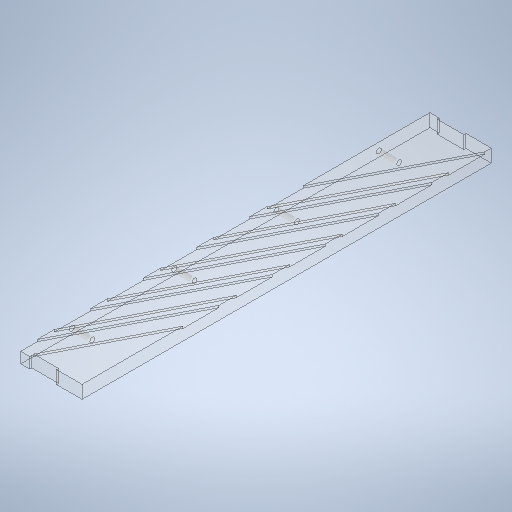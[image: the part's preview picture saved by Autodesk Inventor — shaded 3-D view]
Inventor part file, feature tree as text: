
AUTODESK INVENTOR PART (.ipt)
format: ipt  version: 2025 (Build 290162000, 162)  size: 355,840 bytes
history: native  units: in
note: dims shown in document units (in); Inventor stores cm internally (conversion verified against a paired STEP export)
features: sketch x6, extrude x4, hole x1
ambient origin geometry x8: Origin, YZ Plane, XZ Plane, XY Plane, X Axis, Y Axis, Z Axis, Center Point
bodies: Body1 (feature_tree)
feature tree (11):
  extrude  "Extrusion2"  Depth=7.874in
  extrude  "Extrusion4"  Depth=0.25in
  extrude  "Extrusion6"  Depth=0.0394in TaperAngle=0.0deg
  extrude  "Extrusion7"  Depth=0.3937in
  hole  "Hole1"  [1 undecoded]
  sketch  "Sketch3"  dims[d9=0.25in d10=0.0in d23=0.1855in]
  sketch  "Sketch5"  dims[d25=0.315in d33=0.0394in d34=0.0in]
  sketch  "Sketch Rectangular Pattern1"  dims[d7=1.1811in d8=7.874in]
  sketch  "Sketch7"  dims[d35=0.315in d36=2.3622in d38=1.0236in d39=0.3937in d41=0.3937in]
  sketch  "Sketch8"  dims[d49=0.1772in d50=0.689in]
  sketch  "Sketch9"  dims[d51=0.0394in d52=0.0in d53=0.1772in d54=0.689in d55=0.0394in d56=0.0in d57=0.1053in d58=0.9843in d59=1.9685in d60=0.9843in d61=1.9685in d62=0.0968in d63=0.2953in d64=0.1575in d65=0.0787in d66=90.0deg d67=0.3937in d68=0.8108in]
note: 1 required parameter value undecoded (feature->parameter linkage not recoverable at this tier; creation-order binding heuristic only, values carry confidence <= 0.55)
